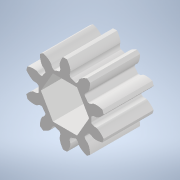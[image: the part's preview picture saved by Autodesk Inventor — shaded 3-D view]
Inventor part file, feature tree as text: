
AUTODESK INVENTOR PART (.ipt)
format: ipt  version: 2022 (Build 260153000, 153)  size: 905,728 bytes
history: native  units: mm
features: extrude x2, sketch x2
ambient origin geometry x8: Origin, YZ Plane, XZ Plane, XY Plane, X Axis, Y Axis, Z Axis, Center Point
bodies: Solid1 (feature_tree)
feature tree (4):
  extrude  "Extrusion1"  Depth=7.5mm
  extrude  "Extrusion2"  Depth=8.0mm TaperAngle=0.0deg
  sketch  "Sketch1"  dims[d0=7.5mm d1=0.0mm d2=3.1mm]
  sketch  "Sketch2"  dims[d3=60.0mm d5=360.0deg d7=8.0mm d8=0.0mm d9=0.45mm]
